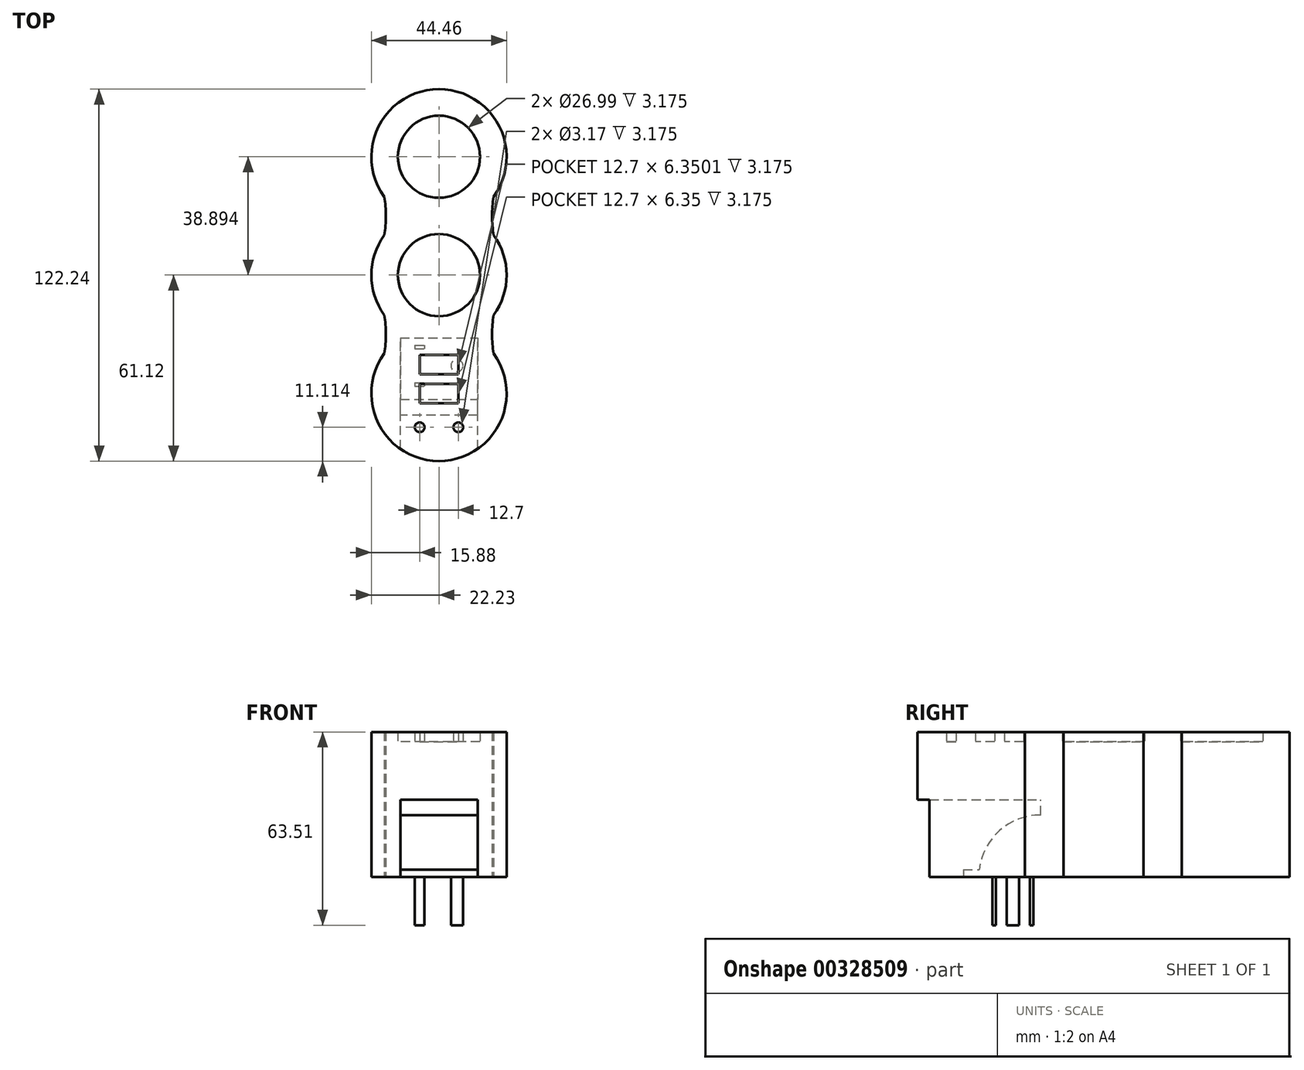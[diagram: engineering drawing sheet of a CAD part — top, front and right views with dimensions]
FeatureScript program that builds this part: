
annotation { "Feature Type Name" : "Feature", "Feature Type Description" : "" }
export const myFeature = defineFeature(function(context is Context, id is Id, definition is map)
    precondition{}
    {
        {
            var Q0;
            Q0=qCreatedBy(makeId("Top.planeOp"),FACE);
            var sketch = newSketch(context, id + "F0", { "sketchPlane" : qUnion([Q0])});
            skPoint(sketch, "E0.middle", {"position": v(0, 0) * mm});
            skCircle(sketch, "E1", {"center": v(0, 0) * mm, "radius": 13.5 * mm});
            skLineSegment(sketch, "E2", {"start": v(0, 61.12) * mm, "end": v(0, 38.9) * mm, "construction": true});
            skPoint(sketch, "E2.endSnap0", {"position": v(0, 61.12) * mm});
            skCircle(sketch, "E3", {"center": v(0, 38.9) * mm, "radius": 13.5 * mm});
            skArc(sketch, "E4", {"start": v(17.94, -13.12) * mm, "mid": v(22.22, 0) * mm, "end": v(17.94, 13.12) * mm});
            skArc(sketch, "E5", {"start": v(17.94, 25.78) * mm, "mid": v(0, 61.12) * mm, "end": v(-17.94, 25.78) * mm});
            skLineSegment(sketch, "E6", {"start": v(0, -61.12) * mm, "end": v(0, -38.9) * mm, "construction": true});
            skPoint(sketch, "E6.endSnap0", {"position": v(0, -61.12) * mm});
            skArc(sketch, "E7", {"start": v(-17.94, -25.78) * mm, "mid": v(0, -61.12) * mm, "end": v(17.94, -25.78) * mm});
            skLineSegment(sketch, "E8", {"start": v(0, 0) * mm, "end": v(0, 38.9) * mm, "construction": true});
            skLineSegment(sketch, "E9", {"start": v(0, 0) * mm, "end": v(0, -38.9) * mm, "construction": true});
            skPoint(sketch, "E10", {"position": v(-10.76, -19.45) * mm});
            skPoint(sketch, "E11", {"position": v(10.76, -19.45) * mm});
            skPoint(sketch, "E12", {"position": v(10.76, 19.45) * mm});
            skPoint(sketch, "E13", {"position": v(-10.76, 19.45) * mm});
            skLineSegment(sketch, "E14", {"start": v(-10.76, 19.45) * mm, "end": v(10.76, 19.45) * mm, "construction": true});
            skLineSegment(sketch, "E15", {"start": v(-10.76, -19.45) * mm, "end": v(10.76, -19.45) * mm, "construction": true});
            skPoint(sketch, "E16", {"position": v(0, -19.45) * mm});
            skPoint(sketch, "E17", {"position": v(0, 19.45) * mm});
            skLineSegment(sketch, "E18", {"start": v(0, -19.45) * mm, "end": v(17.46, -19.45) * mm, "construction": true});
            skLineSegment(sketch, "E19", {"start": v(0, -19.45) * mm, "end": v(-17.46, -19.45) * mm, "construction": true});
            skPoint(sketch, "E20", {"position": v(-22.23, 0) * mm});
            skPoint(sketch, "E21", {"position": v(-22.23, -38.9) * mm});
            skPoint(sketch, "E22", {"position": v(22.22, -38.9) * mm});
            skPoint(sketch, "E23", {"position": v(22.22, 0) * mm});
            skPoint(sketch, "E24", {"position": v(-22.23, 38.9) * mm});
            skPoint(sketch, "E25", {"position": v(22.22, 38.9) * mm});
            skLineSegment(sketch, "E26", {"start": v(-22.23, 0) * mm, "end": v(22.22, 0) * mm, "construction": true});
            skLineSegment(sketch, "E27.MirrorCS", {"start": v(0, 19.45) * mm, "end": v(-17.46, 19.45) * mm, "construction": true});
            skLineSegment(sketch, "E28.MirrorCS", {"start": v(0, 19.45) * mm, "end": v(17.46, 19.45) * mm, "construction": true});
            skArc(sketch, "E29", {"start": v(17.94, -13.12) * mm, "mid": v(17.46, -19.45) * mm, "end": v(17.94, -25.78) * mm});
            skArc(sketch, "E30", {"start": v(17.94, 25.78) * mm, "mid": v(17.46, 19.45) * mm, "end": v(17.94, 13.12) * mm});
            skArc(sketch, "E31", {"start": v(-17.94, 13.12) * mm, "mid": v(-17.46, 19.45) * mm, "end": v(-17.94, 25.78) * mm});
            skArc(sketch, "E32", {"start": v(-17.94, -25.78) * mm, "mid": v(-17.46, -19.45) * mm, "end": v(-17.94, -13.12) * mm});
            skPoint(sketch, "E33.orphan", {"position": v(22.23, 61.12) * mm});
            skPoint(sketch, "E0.left.start.orphan", {"position": v(-22.22, 61.12) * mm});
            skPoint(sketch, "E34.orphan", {"position": v(22.22, -61.12) * mm});
            skPoint(sketch, "E35.trimOffspring.end.orphan", {"position": v(-22.23, -61.12) * mm});
            skArc(sketch, "E36.trimOffspring", {"start": v(-17.94, 13.12) * mm, "mid": v(-22.22, 0) * mm, "end": v(-17.94, -13.12) * mm});
            skLineSegment(sketch, "E37", {"start": v(0, -61.12) * mm, "end": v(0, -26.2) * mm, "construction": true});
            skLineSegment(sketch, "E38", {"start": v(0, -26.2) * mm, "end": v(6.35, -26.2) * mm, "construction": true});
            skLineSegment(sketch, "E39", {"start": v(6.35, -26.2) * mm, "end": v(6.35, -32.54) * mm, "construction": true});
            skLineSegment(sketch, "E40", {"start": v(6.35, -32.54) * mm, "end": v(-6.35, -32.54) * mm, "construction": true});
            skLineSegment(sketch, "E41", {"start": v(-6.35, -32.54) * mm, "end": v(-6.35, -26.2) * mm, "construction": true});
            skLineSegment(sketch, "E42", {"start": v(-6.35, -26.2) * mm, "end": v(0, -26.2) * mm, "construction": true});
            skLineSegment(sketch, "E43", {"start": v(0, -32.54) * mm, "end": v(0, -35.72) * mm, "construction": true});
            skLineSegment(sketch, "E44", {"start": v(0, -35.72) * mm, "end": v(6.35, -35.72) * mm, "construction": true});
            skLineSegment(sketch, "E45", {"start": v(6.35, -35.72) * mm, "end": v(6.35, -42.07) * mm, "construction": true});
            skLineSegment(sketch, "E46", {"start": v(6.35, -42.07) * mm, "end": v(-6.35, -42.07) * mm, "construction": true});
            skLineSegment(sketch, "E47", {"start": v(-6.35, -42.07) * mm, "end": v(-6.35, -35.72) * mm, "construction": true});
            skLineSegment(sketch, "E48", {"start": v(-6.35, -35.72) * mm, "end": v(0, -35.72) * mm, "construction": true});
            skPoint(sketch, "E49", {"position": v(6.35, -50) * mm});
            skPoint(sketch, "E49.positionSnap0", {"position": v(0, -50) * mm});
            skPoint(sketch, "E50", {"position": v(-6.35, -50) * mm});
            skCircle(sketch, "E51", {"center": v(6.35, -50) * mm, "radius": 1.59 * mm});
            skCircle(sketch, "E52", {"center": v(-6.35, -50) * mm, "radius": 1.59 * mm});
            skLineSegment(sketch, "E53.bottom", {"start": v(-6.35, -26.2) * mm, "end": v(6.35, -26.2) * mm});
            skLineSegment(sketch, "E53.top", {"start": v(-6.35, -32.54) * mm, "end": v(6.35, -32.54) * mm});
            skLineSegment(sketch, "E53.left", {"start": v(-6.35, -26.2) * mm, "end": v(-6.35, -32.54) * mm});
            skLineSegment(sketch, "E53.right", {"start": v(6.35, -26.2) * mm, "end": v(6.35, -32.54) * mm});
            skLineSegment(sketch, "E54.bottom", {"start": v(-6.35, -35.72) * mm, "end": v(6.35, -35.72) * mm});
            skLineSegment(sketch, "E54.top", {"start": v(-6.35, -42.07) * mm, "end": v(6.35, -42.07) * mm});
            skLineSegment(sketch, "E54.left", {"start": v(-6.35, -35.72) * mm, "end": v(-6.35, -42.07) * mm});
            skLineSegment(sketch, "E54.right", {"start": v(6.35, -35.72) * mm, "end": v(6.35, -42.07) * mm});
            skSolve(sketch);
        }
        {
            var Q0;
            Q0 = qSketchRegion(id + "F0", true);
            extrude(context, id + "F1", {"entities" : qUnion([Q0]), "depth" : 3.17 * mm});
        }
        {
            var Q0;
            Q0=makeQuery(id+"F0.imprint","IMPRINT",FACE,{"disambiguationData":[TD([[makeQuery(id+"F0.imprint","IMPRINT",EDGE,{"derivedFrom":sQuery(id+"F0.wireOp",EDGE,"E1")}),-1.0]])]});
            var Q1;
            Q1=makeQuery(id+"F0.imprint","IMPRINT",FACE,{"disambiguationData":[TD([[makeQuery(id+"F0.imprint","IMPRINT",EDGE,{"derivedFrom":sQuery(id+"F0.wireOp",EDGE,"E51")}),1.0]])]});
            var Q2;
            Q2=makeQuery(id+"F0.imprint","IMPRINT",FACE,{"disambiguationData":[TD([[makeQuery(id+"F0.imprint","IMPRINT",EDGE,{"derivedFrom":sQuery(id+"F0.wireOp",EDGE,"E52")}),1.0]])]});
            var Q3;
            Q3=makeQuery(id+"F0.imprint","IMPRINT",FACE,{"disambiguationData":[TD([[makeQuery(id+"F0.imprint","IMPRINT",EDGE,{"derivedFrom":sQuery(id+"F0.wireOp",EDGE,"E54.bottom")}),-1.0]])]});
            var Q4;
            Q4=makeQuery(id+"F0.imprint","IMPRINT",FACE,{"disambiguationData":[TD([[makeQuery(id+"F0.imprint","IMPRINT",EDGE,{"derivedFrom":sQuery(id+"F0.wireOp",EDGE,"E53.bottom")}),-1.0]])]});
            var Q5;
            Q5=makeQuery(id+"F0.imprint","IMPRINT",FACE,{"disambiguationData":[TD([[makeQuery(id+"F0.imprint","IMPRINT",EDGE,{"derivedFrom":sQuery(id+"F0.wireOp",EDGE,"E1")}),1.0]])]});
            var Q6;
            Q6=makeQuery(id+"F0.imprint","IMPRINT",FACE,{"disambiguationData":[TD([[makeQuery(id+"F0.imprint","IMPRINT",EDGE,{"derivedFrom":sQuery(id+"F0.wireOp",EDGE,"E3")}),1.0]])]});
            extrude(context, id + "F2", {"entities" : qUnion([Q0, Q1, Q2, Q3, Q4, Q5, Q6]), "operationType" : NewBodyOperationType.ADD, "oppositeDirection" : true, "depth" : 19.05 * mm});
        }
        {
            var Q0;
            Q0=makeQuery(id+"F2.opExtrude","CAP_FACE",FACE,{"disambiguationData":[OSD([sQuery(id+"F0.wireOp",EDGE,"E4"),sQuery(id+"F0.wireOp",EDGE,"E5"),sQuery(id+"F0.wireOp",EDGE,"E7"),sQuery(id+"F0.wireOp",EDGE,"E29"),sQuery(id+"F0.wireOp",EDGE,"E30"),sQuery(id+"F0.wireOp",EDGE,"E31"),sQuery(id+"F0.wireOp",EDGE,"E32"),sQuery(id+"F0.wireOp",EDGE,"E36.trimOffspring")])],"isStart":false});
            var sketch = newSketch(context, id + "F3", { "sketchPlane" : qUnion([Q0])});
            skLineSegment(sketch, "E55", {"start": v(0, 61.12) * mm, "end": v(0, 57.15) * mm, "construction": true});
            skPoint(sketch, "E55.endSnap0", {"position": v(0, 61.12) * mm});
            skLineSegment(sketch, "E56", {"start": v(12.68, 57.15) * mm, "end": v(12.68, 20.64) * mm});
            skLineSegment(sketch, "E57", {"start": v(-12.68, 57.15) * mm, "end": v(-12.68, 20.64) * mm});
            skLineSegment(sketch, "E58", {"start": v(-12.68, 20.64) * mm, "end": v(12.68, 20.64) * mm});
            skPoint(sketch, "E59", {"position": v(-12.68, 57.15) * mm});
            skPoint(sketch, "E60", {"position": v(12.68, 57.15) * mm});
            skLineSegment(sketch, "E61", {"start": v(12.68, 20.64) * mm, "end": v(12.68, 46.04) * mm});
            skLineSegment(sketch, "E62", {"start": v(12.68, 46.04) * mm, "end": v(-12.68, 46.04) * mm});
            skLineSegment(sketch, "E63", {"start": v(-12.68, 46.04) * mm, "end": v(-12.68, 40.96) * mm});
            skLineSegment(sketch, "E64", {"start": v(-12.68, 40.96) * mm, "end": v(12.68, 40.96) * mm});
            skSolve(sketch);
        }
        {
            var Q0;
            {var subQ2=sQuery(id+"F3.wireOp",EDGE,"E56");Q0=makeQuery(id+"F3.imprint","IMPRINT",FACE,{"disambiguationData":[TD([[makeQuery(id+"F3.imprint","IMPRINT",EDGE,{"derivedFrom":subQ2}),1.0]])]});}
            extrude(context, id + "F4", {"entities" : qUnion([Q0]), "operationType" : NewBodyOperationType.ADD, "depth" : 25.4 * mm});
        }
        {
            var Q0;
            Q0=makeQuery(id+"F4.opExtrude","CAP_FACE",FACE,{"disambiguationData":[OSD([sQuery(id+"F0.wireOp",EDGE,"E4"),sQuery(id+"F0.wireOp",EDGE,"E5"),sQuery(id+"F0.wireOp",EDGE,"E7"),sQuery(id+"F0.wireOp",EDGE,"E29"),sQuery(id+"F0.wireOp",EDGE,"E30"),sQuery(id+"F0.wireOp",EDGE,"E31"),sQuery(id+"F0.wireOp",EDGE,"E32"),sQuery(id+"F0.wireOp",EDGE,"E36.trimOffspring"),sQuery(id+"F3.wireOp",EDGE,"E56"),sQuery(id+"F3.wireOp",EDGE,"E57"),sQuery(id+"F3.wireOp",EDGE,"E58"),sQuery(id+"F3.wireOp",EDGE,"E61"),sQuery(id+"F3.wireOp",EDGE,"E63")])],"isStart":false});
            var sketch = newSketch(context, id + "F5", { "sketchPlane" : qUnion([Q0])});
            skLineSegment(sketch, "E65.0.0", {"start": v(-12.68, 20.64) * mm, "end": v(-12.68, 57.15) * mm});
            skArc(sketch, "E65.0.1", {"start": v(-12.68, 57.15) * mm, "mid": v(-21.92, 42.57) * mm, "end": v(-17.94, 25.78) * mm});
            skArc(sketch, "E65.0.2", {"start": v(-17.94, 25.78) * mm, "mid": v(-17.46, 19.45) * mm, "end": v(-17.94, 13.12) * mm});
            skArc(sketch, "E65.0.3", {"start": v(-17.94, 13.12) * mm, "mid": v(-22.22, 0) * mm, "end": v(-17.94, -13.12) * mm});
            skArc(sketch, "E65.0.4", {"start": v(-17.94, -13.12) * mm, "mid": v(-17.46, -19.45) * mm, "end": v(-17.94, -25.78) * mm});
            skArc(sketch, "E65.0.5", {"start": v(-17.94, -25.78) * mm, "mid": v(0, -61.12) * mm, "end": v(17.94, -25.78) * mm});
            skArc(sketch, "E65.0.6", {"start": v(17.94, -25.78) * mm, "mid": v(17.46, -19.45) * mm, "end": v(17.94, -13.12) * mm});
            skArc(sketch, "E65.0.7", {"start": v(17.94, -13.12) * mm, "mid": v(22.22, 0) * mm, "end": v(17.94, 13.12) * mm});
            skArc(sketch, "E65.0.8", {"start": v(17.94, 13.12) * mm, "mid": v(17.46, 19.45) * mm, "end": v(17.94, 25.78) * mm});
            skArc(sketch, "E65.0.9", {"start": v(17.94, 25.78) * mm, "mid": v(21.92, 42.57) * mm, "end": v(12.68, 57.15) * mm});
            skLineSegment(sketch, "E65.0.10", {"start": v(12.68, 57.15) * mm, "end": v(12.68, 20.64) * mm});
            skLineSegment(sketch, "E65.0.11", {"start": v(12.68, 20.64) * mm, "end": v(-12.68, 20.64) * mm});
            skLineSegment(sketch, "E66.0", {"start": v(-12.68, 40.96) * mm, "end": v(12.68, 40.96) * mm});
            skLineSegment(sketch, "E67.0", {"start": v(12.68, 46.04) * mm, "end": v(-12.68, 46.04) * mm});
            skLineSegment(sketch, "E68", {"start": v(-12.68, 38.9) * mm, "end": v(12.68, 38.9) * mm});
            skSolve(sketch);
        }
        {
            var Q0;
            {var subQ0=sQuery(id+"F5.wireOp",EDGE,"E65.0.11");Q0=makeQuery(id+"F5.imprint","IMPRINT",FACE,{"disambiguationData":[TD([[makeQuery(id+"F5.imprint","IMPRINT",EDGE,{"derivedFrom":subQ0}),1.0]])]});}
            var Q1;
            {var subQ0=sQuery(id+"F5.wireOp",EDGE,"E66.0");Q1=makeQuery(id+"F5.imprint","IMPRINT",FACE,{"disambiguationData":[TD([[makeQuery(id+"F5.imprint","IMPRINT",EDGE,{"derivedFrom":subQ0}),-1.0]])]});}
            var Q2;
            Q2=sQuery(id+"F5.wireOp",EDGE,"E65.0.11");
            revolve(context, id + "F6", {"operationType" : NewBodyOperationType.ADD, "entities" : qUnion([Q0, Q1]), "axis" : qUnion([Q2]), "revolveType" : RevolveType.ONE_DIRECTION, "angle" : 90 * degree});
        }
        {
            var Q0;
            {var subQ0=sQuery(id+"F5.wireOp",EDGE,"E66.0");Q0=makeQuery(id+"F5.imprint","IMPRINT",FACE,{"disambiguationData":[TD([[makeQuery(id+"F5.imprint","IMPRINT",EDGE,{"derivedFrom":subQ0}),-1.0]])]});}
            var Q1;
            {var subQ0=sQuery(id+"F5.wireOp",EDGE,"E66.0");Q1=makeQuery(id+"F5.imprint","IMPRINT",FACE,{"disambiguationData":[TD([[makeQuery(id+"F5.imprint","IMPRINT",EDGE,{"derivedFrom":subQ0}),1.0]])]});}
            extrude(context, id + "F7", {"entities" : qUnion([Q0, Q1]), "operationType" : NewBodyOperationType.ADD, "oppositeDirection" : true, "depth" : 2.38 * mm});
        }
        {
            var Q0;
            {var subQ0=sQuery(id+"F5.wireOp",EDGE,"E65.0.1");Q0=makeQuery(id+"F5.imprint","IMPRINT",FACE,{"disambiguationData":[TD([[makeQuery(id+"F5.imprint","IMPRINT",EDGE,{"derivedFrom":subQ0}),-1.0]])]});}
            var sketch = newSketch(context, id + "F8", { "sketchPlane" : qUnion([Q0])});
            skLineSegment(sketch, "E69.0.0", {"start": v(12.68, 38.9) * mm, "end": v(-12.68, 38.9) * mm});
            skLineSegment(sketch, "E69.0.1", {"start": v(-12.68, 38.9) * mm, "end": v(-12.68, 20.64) * mm});
            skLineSegment(sketch, "E69.0.2", {"start": v(-12.68, 20.64) * mm, "end": v(12.68, 20.64) * mm});
            skLineSegment(sketch, "E69.0.3", {"start": v(12.68, 20.64) * mm, "end": v(12.68, 38.9) * mm});
            skLineSegment(sketch, "E70", {"start": v(-12.68, 38.9) * mm, "end": v(-11.96, 38.9) * mm, "construction": true});
            skLineSegment(sketch, "E71", {"start": v(-12.68, 20.64) * mm, "end": v(-12.68, 23.02) * mm, "construction": true});
            skLineSegment(sketch, "E72", {"start": v(-12.68, 23.02) * mm, "end": v(-12.68, 24.2) * mm, "construction": true});
            skLineSegment(sketch, "E73", {"start": v(-12.68, 24.2) * mm, "end": v(-12.68, 35.32) * mm, "construction": true});
            skLineSegment(sketch, "E74", {"start": v(-12.68, 35.32) * mm, "end": v(-12.68, 36.51) * mm, "construction": true});
            skLineSegment(sketch, "E75", {"start": v(-12.68, 38.9) * mm, "end": v(-7.91, 38.9) * mm});
            skLineSegment(sketch, "E76", {"start": v(-7.91, 36.51) * mm, "end": v(-7.91, 35.32) * mm, "construction": true});
            skLineSegment(sketch, "E77", {"start": v(-7.91, 38.9) * mm, "end": v(-4.74, 38.9) * mm, "construction": true});
            skLineSegment(sketch, "E78", {"start": v(-4.74, 36.51) * mm, "end": v(-4.74, 35.32) * mm, "construction": true});
            skLineSegment(sketch, "E79", {"start": v(-7.91, 23.02) * mm, "end": v(-4.74, 23.02) * mm});
            skLineSegment(sketch, "E80", {"start": v(-7.91, 24.2) * mm, "end": v(-4.74, 24.2) * mm});
            skLineSegment(sketch, "E81", {"start": v(-7.91, 35.32) * mm, "end": v(-4.74, 35.32) * mm});
            skLineSegment(sketch, "E82", {"start": v(-7.91, 36.51) * mm, "end": v(-4.74, 36.51) * mm});
            skLineSegment(sketch, "E83.trimOffspring", {"start": v(-7.91, 24.2) * mm, "end": v(-7.91, 23.02) * mm, "construction": true});
            skLineSegment(sketch, "E84.trimOffspring", {"start": v(-4.74, 24.2) * mm, "end": v(-4.74, 23.02) * mm, "construction": true});
            skLineSegment(sketch, "E85", {"start": v(-7.91, 23.02) * mm, "end": v(-7.91, 24.2) * mm});
            skLineSegment(sketch, "E86", {"start": v(-7.91, 35.32) * mm, "end": v(-7.91, 36.51) * mm});
            skLineSegment(sketch, "E87", {"start": v(-4.74, 35.32) * mm, "end": v(-4.74, 36.51) * mm});
            skLineSegment(sketch, "E88", {"start": v(-4.74, 23.02) * mm, "end": v(-4.74, 24.2) * mm});
            skLineSegment(sketch, "E89", {"start": v(12.68, 29.77) * mm, "end": v(7.91, 29.77) * mm, "construction": true});
            skLineSegment(sketch, "E90", {"start": v(7.91, 29.77) * mm, "end": v(7.91, 20.64) * mm, "construction": true});
            skLineSegment(sketch, "E91", {"start": v(7.91, 20.64) * mm, "end": v(7.91, 29.77) * mm, "construction": true});
            skLineSegment(sketch, "E92", {"start": v(7.91, 29.77) * mm, "end": v(5.93, 29.77) * mm, "construction": true});
            skCircle(sketch, "E93", {"center": v(5.93, 29.77) * mm, "radius": 1.98 * mm});
            skPoint(sketch, "E94", {"position": v(-12.68, 29.77) * mm});
            skSolve(sketch);
        }
        {
            var Q0;
            Q0=makeQuery(id+"F8.imprint","IMPRINT",FACE,{"disambiguationData":[TD([[makeQuery(id+"F8.imprint","IMPRINT",EDGE,{"derivedFrom":sQuery(id+"F8.wireOp",EDGE,"E79")}),1.0]])]});
            var Q1;
            Q1=makeQuery(id+"F8.imprint","IMPRINT",FACE,{"disambiguationData":[TD([[makeQuery(id+"F8.imprint","IMPRINT",EDGE,{"derivedFrom":sQuery(id+"F8.wireOp",EDGE,"E81")}),1.0]])]});
            var Q2;
            Q2=makeQuery(id+"F8.imprint","IMPRINT",FACE,{"disambiguationData":[TD([[makeQuery(id+"F8.imprint","IMPRINT",EDGE,{"derivedFrom":sQuery(id+"F8.wireOp",EDGE,"E93")}),1.0]])]});
            var Q3;
            Q3=sQuery(id+"F8.wireOp",EDGE,"E93");
            extrude(context, id + "F9", {"entities" : qUnion([Q0, Q1, Q2]), "operationType" : NewBodyOperationType.ADD, "surfaceEntities" : qUnion([Q3]), "depth" : 15.88 * mm});
        }
    });
